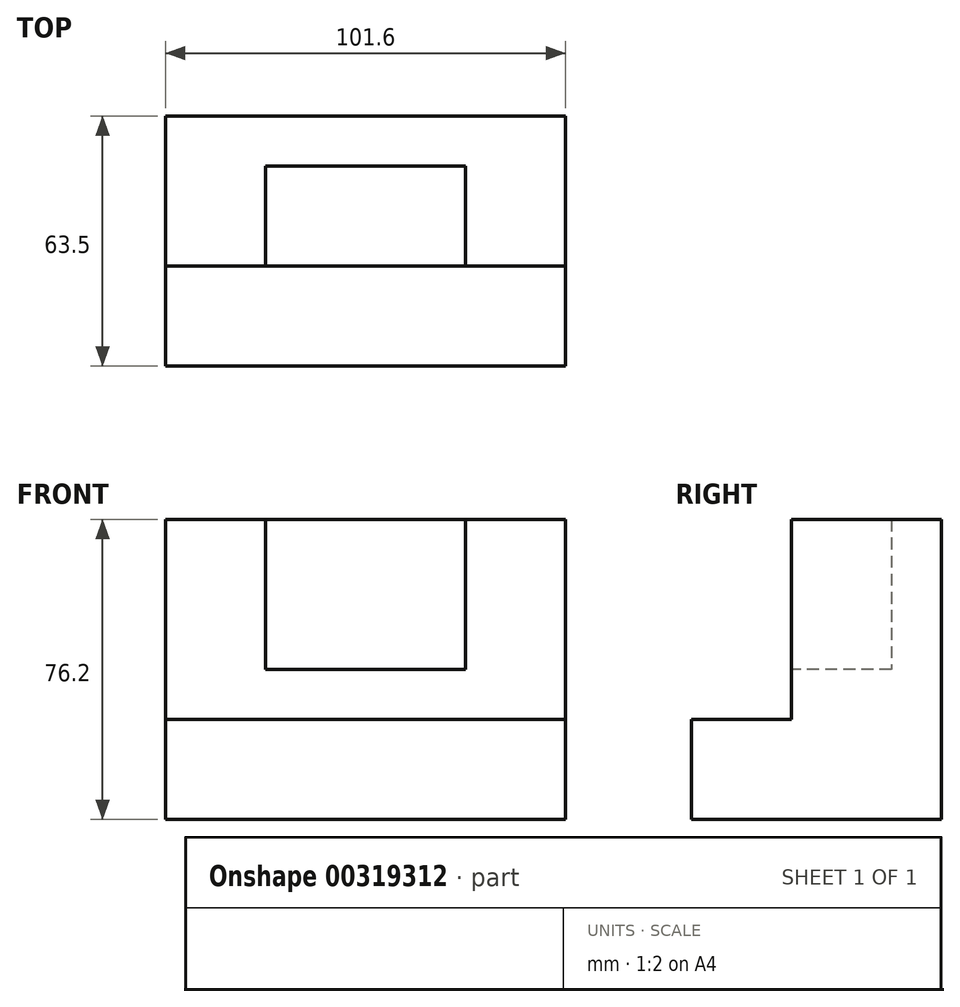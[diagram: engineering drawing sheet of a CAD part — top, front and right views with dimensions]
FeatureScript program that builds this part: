
annotation { "Feature Type Name" : "Feature", "Feature Type Description" : "" }
export const myFeature = defineFeature(function(context is Context, id is Id, definition is map)
    precondition{}
    {
        {
            var Q0;
            Q0=qCreatedBy(makeId("Top.planeOp"),FACE);
            var sketch = newSketch(context, id + "F0", { "sketchPlane" : qUnion([Q0])});
            skLineSegment(sketch, "E0", {"start": v(-43.84, -33.4) * mm, "end": v(57.76, -33.4) * mm});
            skLineSegment(sketch, "E1", {"start": v(57.76, -33.4) * mm, "end": v(57.76, 30.1) * mm});
            skLineSegment(sketch, "E2", {"start": v(57.76, 30.1) * mm, "end": v(-43.84, 30.1) * mm});
            skLineSegment(sketch, "E3", {"start": v(-43.84, 30.1) * mm, "end": v(-43.84, -33.4) * mm});
            skSolve(sketch);
        }
        {
            var Q0;
            Q0=makeQuery(id+"F0.imprint","IMPRINT",FACE,{"disambiguationData":[TD([[makeQuery(id+"F0.imprint","IMPRINT",EDGE,{"derivedFrom":sQuery(id+"F0.wireOp",EDGE,"E0")}),1.0]])]});
            extrude(context, id + "F1", {"entities" : qUnion([Q0]), "depth" : 25.4 * mm});
        }
        {
            var Q0;
            Q0=makeQuery(id+"F1.opExtrude","CAP_FACE",FACE,{"disambiguationData":[OSD([sQuery(id+"F0.wireOp",EDGE,"E0"),sQuery(id+"F0.wireOp",EDGE,"E1"),sQuery(id+"F0.wireOp",EDGE,"E2"),sQuery(id+"F0.wireOp",EDGE,"E3")])],"isStart":false});
            var sketch = newSketch(context, id + "F2", { "sketchPlane" : qUnion([Q0])});
            skLineSegment(sketch, "E4", {"start": v(-43.84, 30.1) * mm, "end": v(57.76, 30.1) * mm});
            skLineSegment(sketch, "E5", {"start": v(57.76, 30.1) * mm, "end": v(57.76, -8) * mm});
            skLineSegment(sketch, "E6", {"start": v(57.76, -8) * mm, "end": v(32.36, -8) * mm});
            skLineSegment(sketch, "E7", {"start": v(32.36, -8) * mm, "end": v(32.36, 17.4) * mm});
            skLineSegment(sketch, "E8", {"start": v(32.36, 17.4) * mm, "end": v(-18.44, 17.4) * mm});
            skLineSegment(sketch, "E9", {"start": v(-18.44, 17.4) * mm, "end": v(-18.44, -8) * mm});
            skLineSegment(sketch, "E10", {"start": v(-18.44, -8) * mm, "end": v(-43.84, -8) * mm});
            skLineSegment(sketch, "E11", {"start": v(-43.84, -8) * mm, "end": v(-43.84, 30.1) * mm});
            skSolve(sketch);
        }
        {
            var Q0;
            Q0=makeQuery(id+"F2.imprint","IMPRINT",FACE,{"disambiguationData":[TD([[makeQuery(id+"F2.imprint","IMPRINT",EDGE,{"derivedFrom":sQuery(id+"F2.wireOp",EDGE,"E4")}),1.0]])]});
            extrude(context, id + "F3", {"entities" : qUnion([Q0]), "operationType" : NewBodyOperationType.ADD, "depth" : 50.8 * mm});
        }
        {
            var Q0;
            Q0=makeQuery(id+"F1.opExtrude","CAP_FACE",FACE,{"disambiguationData":[OSD([sQuery(id+"F0.wireOp",EDGE,"E0"),sQuery(id+"F0.wireOp",EDGE,"E1"),sQuery(id+"F0.wireOp",EDGE,"E2"),sQuery(id+"F0.wireOp",EDGE,"E3")])],"isStart":false});
            var sketch = newSketch(context, id + "F4", { "sketchPlane" : qUnion([Q0])});
            skLineSegment(sketch, "E12", {"start": v(-18.44, 17.4) * mm, "end": v(-18.44, -8) * mm});
            skLineSegment(sketch, "E13", {"start": v(-18.44, -8) * mm, "end": v(32.36, -8) * mm});
            skLineSegment(sketch, "E14", {"start": v(32.36, -8) * mm, "end": v(32.36, 17.4) * mm});
            skLineSegment(sketch, "E15", {"start": v(32.36, 17.4) * mm, "end": v(-18.44, 17.4) * mm});
            skSolve(sketch);
        }
        {
            var Q0;
            Q0=makeQuery(id+"F4.imprint","IMPRINT",FACE,{"disambiguationData":[TD([[makeQuery(id+"F4.imprint","IMPRINT",EDGE,{"derivedFrom":sQuery(id+"F4.wireOp",EDGE,"E12")}),1.0]])]});
            extrude(context, id + "F5", {"entities" : qUnion([Q0]), "operationType" : NewBodyOperationType.ADD, "depth" : 12.7 * mm});
        }
    });
